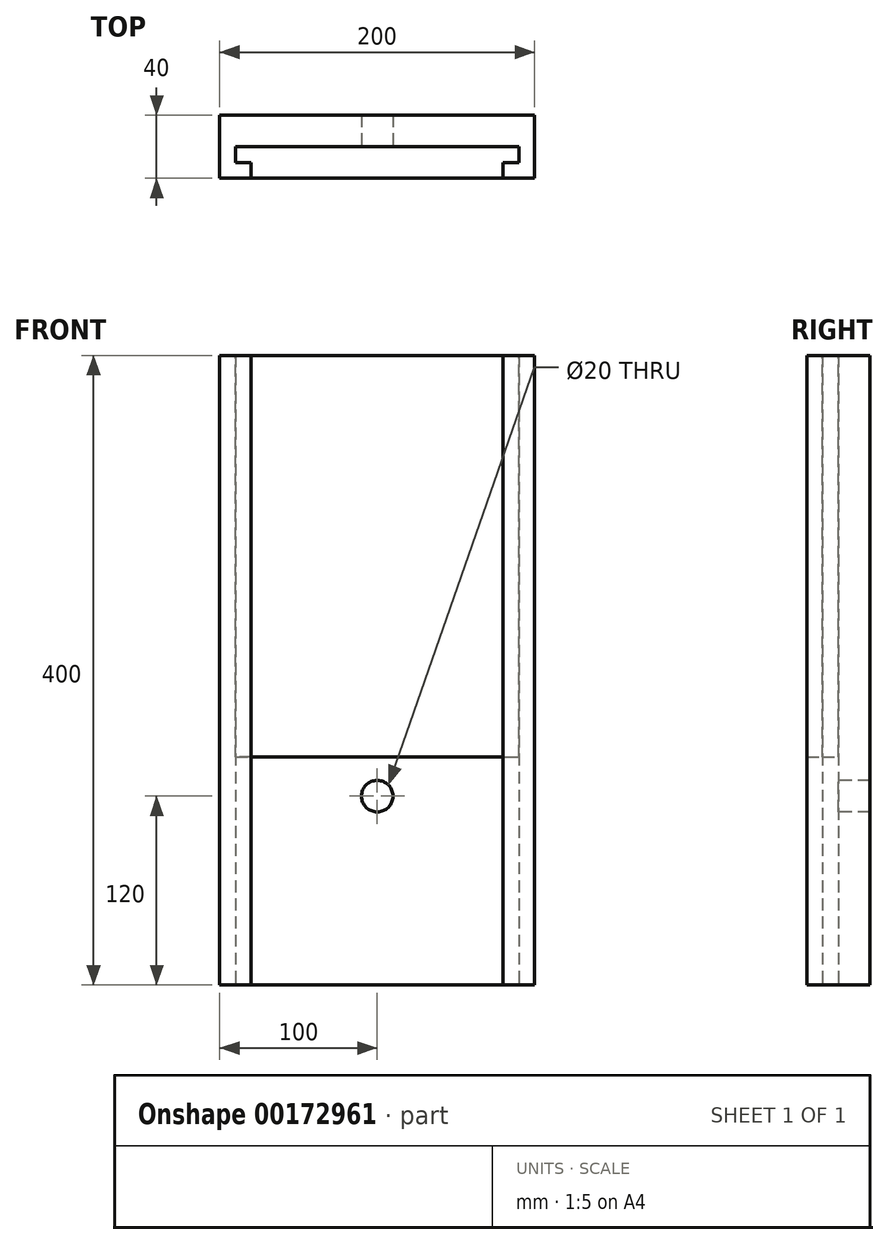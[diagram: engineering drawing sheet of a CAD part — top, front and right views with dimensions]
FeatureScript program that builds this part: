
annotation { "Feature Type Name" : "Feature", "Feature Type Description" : "" }
export const myFeature = defineFeature(function(context is Context, id is Id, definition is map)
    precondition{}
    {
        {
            var Q0;
            Q0=qCreatedBy(makeId("Top.planeOp"),FACE);
            var sketch = newSketch(context, id + "F0", { "sketchPlane" : qUnion([Q0])});
            skLineSegment(sketch, "E0", {"start": v(0, 40) * mm, "end": v(100, 40) * mm});
            skLineSegment(sketch, "E1", {"start": v(100, 40) * mm, "end": v(100, 0) * mm});
            skLineSegment(sketch, "E2", {"start": v(100, 0) * mm, "end": v(80, 0) * mm});
            skLineSegment(sketch, "E3", {"start": v(80, 0) * mm, "end": v(80, 10) * mm});
            skLineSegment(sketch, "E4", {"start": v(80, 10) * mm, "end": v(90, 10) * mm});
            skLineSegment(sketch, "E5", {"start": v(90, 10) * mm, "end": v(90, 20) * mm});
            skLineSegment(sketch, "E6", {"start": v(90, 20) * mm, "end": v(0, 20) * mm});
            skLineSegment(sketch, "E7", {"start": v(0, 0) * mm, "end": v(0, 40) * mm, "construction": true});
            skLineSegment(sketch, "E8.MirrorCS", {"start": v(0, 40) * mm, "end": v(-100, 40) * mm});
            skLineSegment(sketch, "E9.MirrorCS", {"start": v(-90, 20) * mm, "end": v(0, 20) * mm});
            skLineSegment(sketch, "E10.MirrorCS", {"start": v(-90, 10) * mm, "end": v(-90, 20) * mm});
            skLineSegment(sketch, "E11.MirrorCS", {"start": v(-80, 10) * mm, "end": v(-90, 10) * mm});
            skLineSegment(sketch, "E12.MirrorCS", {"start": v(-80, 0) * mm, "end": v(-80, 10) * mm});
            skLineSegment(sketch, "E13.MirrorCS", {"start": v(-100, 0) * mm, "end": v(-80, 0) * mm});
            skLineSegment(sketch, "E14.MirrorCS", {"start": v(-100, 40) * mm, "end": v(-100, 0) * mm});
            skSolve(sketch);
        }
        {
            var Q0;
            Q0 = qSketchRegion(id + "F0", true);
            extrude(context, id + "F1", {"entities" : qUnion([Q0]), "depth" : 280 * mm, "hasSecondDirection" : true, "secondDirectionOppositeDirection" : true, "secondDirectionDepth" : 120 * mm});
        }
        {
            var Q0;
            Q0=makeQuery(id+"F1.opExtrude","SWEPT_FACE",FACE,{"disambiguationData":[OSD([sQuery(id+"F0.wireOp",EDGE,"E6"),sQuery(id+"F0.wireOp",EDGE,"E9.MirrorCS")])]});
            var sketch = newSketch(context, id + "F2", { "sketchPlane" : qUnion([Q0])});
            skCircle(sketch, "E15", {"center": v(0, 0) * mm, "radius": 10 * mm});
            skSolve(sketch);
        }
        {
            var Q0;
            Q0=makeQuery(id+"F2.imprint","IMPRINT",FACE,{"disambiguationData":[TD([[makeQuery(id+"F2.imprint","IMPRINT",EDGE,{"derivedFrom":sQuery(id+"F2.wireOp",EDGE,"E15")}),1.0]])]});
            extrude(context, id + "F3", {"entities" : qUnion([Q0]), "operationType" : NewBodyOperationType.REMOVE, "oppositeDirection" : true, "depth" : 20 * mm});
        }
        {
            var Q0;
            Q0=makeQuery(id+"F1.opExtrude","CAP_FACE",FACE,{"disambiguationData":[OSD([sQuery(id+"F0.wireOp",EDGE,"E0"),sQuery(id+"F0.wireOp",EDGE,"E1"),sQuery(id+"F0.wireOp",EDGE,"E2"),sQuery(id+"F0.wireOp",EDGE,"E3"),sQuery(id+"F0.wireOp",EDGE,"E4"),sQuery(id+"F0.wireOp",EDGE,"E5"),sQuery(id+"F0.wireOp",EDGE,"E6"),sQuery(id+"F0.wireOp",EDGE,"E8.MirrorCS"),sQuery(id+"F0.wireOp",EDGE,"E9.MirrorCS"),sQuery(id+"F0.wireOp",EDGE,"E10.MirrorCS"),sQuery(id+"F0.wireOp",EDGE,"E11.MirrorCS"),sQuery(id+"F0.wireOp",EDGE,"E12.MirrorCS"),sQuery(id+"F0.wireOp",EDGE,"E13.MirrorCS"),sQuery(id+"F0.wireOp",EDGE,"E14.MirrorCS")])],"isStart":false});
            var sketch = newSketch(context, id + "F4", { "sketchPlane" : qUnion([Q0])});
            skLineSegment(sketch, "E16", {"start": v(-90, 20) * mm, "end": v(-90, 10) * mm});
            skLineSegment(sketch, "E17", {"start": v(-90, 10) * mm, "end": v(-80, 10) * mm});
            skLineSegment(sketch, "E18", {"start": v(-80, 10) * mm, "end": v(-80, 0) * mm});
            skLineSegment(sketch, "E19", {"start": v(90, 20) * mm, "end": v(90, 10) * mm});
            skLineSegment(sketch, "E20", {"start": v(90, 10) * mm, "end": v(80, 10) * mm});
            skLineSegment(sketch, "E21", {"start": v(80, 10) * mm, "end": v(80, 0) * mm});
            skLineSegment(sketch, "E22", {"start": v(-80, 0) * mm, "end": v(80, 0) * mm});
            skSolve(sketch);
        }
        {
            var Q0;
            Q0=makeQuery(id+"F4.imprint","IMPRINT",FACE,{"disambiguationData":[TD([[makeQuery(id+"F4.imprint","IMPRINT",EDGE,{"derivedFrom":sQuery(id+"F4.wireOp",EDGE,"E16")}),-1.0]])]});
            extrude(context, id + "F5", {"entities" : qUnion([Q0]), "oppositeDirection" : true, "depth" : 255 * mm});
        }
    });
